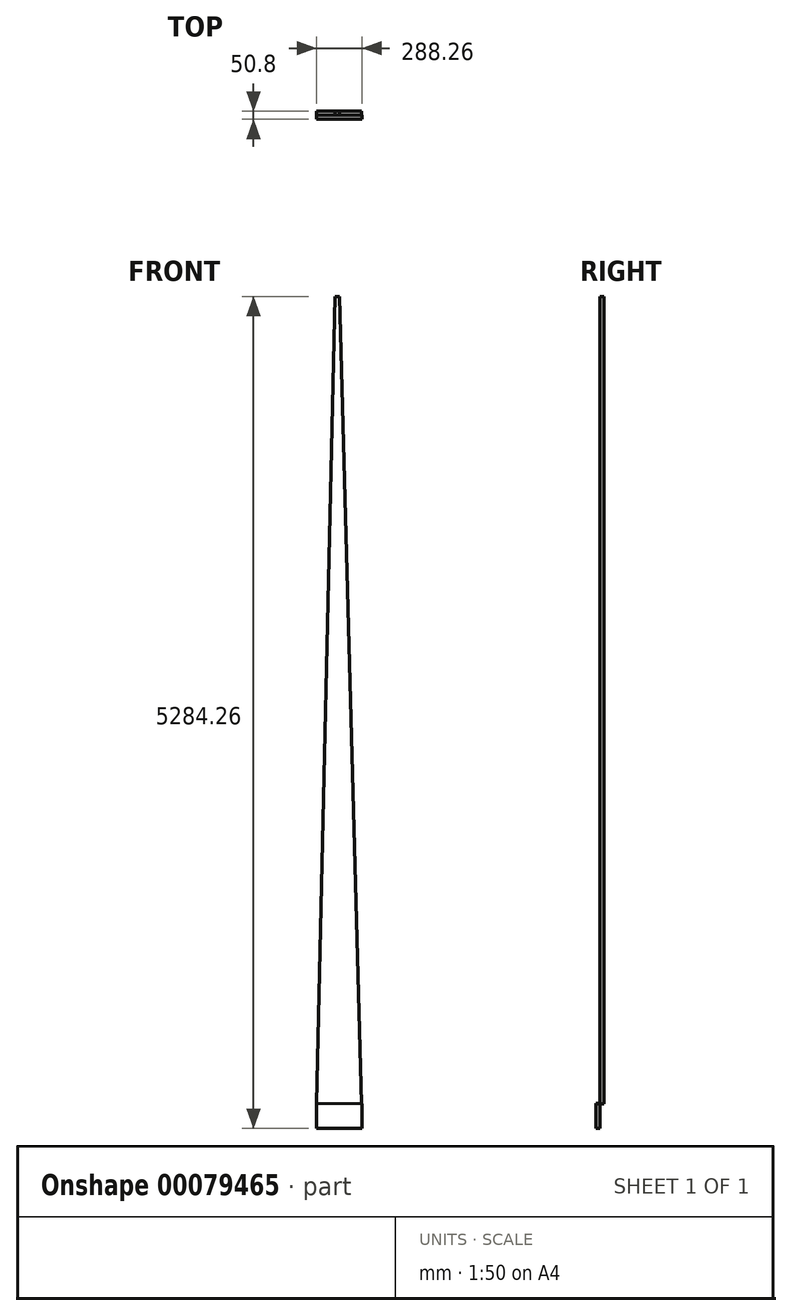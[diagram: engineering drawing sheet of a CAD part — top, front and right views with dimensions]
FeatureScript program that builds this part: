
annotation { "Feature Type Name" : "Feature", "Feature Type Description" : "" }
export const myFeature = defineFeature(function(context is Context, id is Id, definition is map)
    precondition{}
    {
        {
            var Q0;
            Q0=qCreatedBy(makeId("Front.planeOp"),FACE);
            var sketch = newSketch(context, id + "F0", { "sketchPlane" : qUnion([Q0])});
            skLineSegment(sketch, "E0", {"start": v(-145.66, 80.98) * mm, "end": v(-145.66, -77.37) * mm});
            skLineSegment(sketch, "E1", {"start": v(-145.66, -77.37) * mm, "end": v(142.6, -77.37) * mm});
            skLineSegment(sketch, "E2", {"start": v(142.6, -77.37) * mm, "end": v(142.6, 77.56) * mm});
            skLineSegment(sketch, "E3", {"start": v(142.6, 77.56) * mm, "end": v(-145.66, 80.98) * mm});
            skSolve(sketch);
        }
        {
            var Q0;
            Q0=makeQuery(id+"F0.imprint","IMPRINT",FACE,{"disambiguationData":[TD([[makeQuery(id+"F0.imprint","IMPRINT",EDGE,{"derivedFrom":sQuery(id+"F0.wireOp",EDGE,"E0")}),1.0]])]});
            extrude(context, id + "F1", {"entities" : qUnion([Q0]), "depth" : 25.4 * mm});
        }
        {
            var Q0;
            Q0=makeQuery(id+"F1.opExtrude","CAP_FACE",FACE,{"disambiguationData":[OSD([sQuery(id+"F0.wireOp",EDGE,"E0"),sQuery(id+"F0.wireOp",EDGE,"E1"),sQuery(id+"F0.wireOp",EDGE,"E2"),sQuery(id+"F0.wireOp",EDGE,"E3")])],"isStart":true});
            var sketch = newSketch(context, id + "F2", { "sketchPlane" : qUnion([Q0])});
            skLineSegment(sketch, "E4", {"start": v(145.66, 80.98) * mm, "end": v(27.63, 5237.06) * mm});
            skLineSegment(sketch, "E5", {"start": v(1.2, 5206.9) * mm, "end": v(-142.6, -77.37) * mm});
            skLineSegment(sketch, "E6", {"start": v(-142.6, -77.37) * mm, "end": v(28.32, 5206.9) * mm});
            skLineSegment(sketch, "E7", {"start": v(28.32, 5206.9) * mm, "end": v(1.2, 5206.9) * mm});
            skLineSegment(sketch, "E8", {"start": v(145.66, -77.37) * mm, "end": v(1.2, 5206.9) * mm});
            skSolve(sketch);
        }
        {
            var Q0;
            {var subQ0=sQuery(id+"F2.wireOp",EDGE,"E8");var subQ1=sQuery(id+"F2.wireOp",EDGE,"E6");var subQ2=makeQuery(id+"F2.imprint","INTERSECT",VERTEX,{"derivedFrom":[subQ1,subQ0]});Q0=makeQuery(id+"F2.imprint","IMPRINT",FACE,{"disambiguationData":[TD([[makeQuery(id+"F2.imprint","IMPRINT",EDGE,{"disambiguationData":[TD([[subQ2,1.0]])],"derivedFrom":subQ1}),-1.0]])]});}
            var Q1;
            {var subQ0=sQuery(id+"F2.wireOp",EDGE,"E8");var subQ5=sQuery(id+"F2.wireOp",EDGE,"E6");var subQ6=makeQuery(id+"F2.imprint","INTERSECT",VERTEX,{"derivedFrom":[subQ5,subQ0]});Q1=makeQuery(id+"F2.imprint","IMPRINT",FACE,{"disambiguationData":[TD([[makeQuery(id+"F2.imprint","IMPRINT",EDGE,{"disambiguationData":[TD([[subQ6,1.0]])],"derivedFrom":subQ5}),1.0]])]});}
            var Q2;
            {var subQ0=sQuery(id+"F2.wireOp",EDGE,"E7");Q2=makeQuery(id+"F2.imprint","IMPRINT",FACE,{"disambiguationData":[TD([[makeQuery(id+"F2.imprint","IMPRINT",EDGE,{"derivedFrom":subQ0}),1.0]])]});}
            var Q3;
            {var subQ3=sQuery(id+"F2.wireOp",EDGE,"E6");var subQ5=sQuery(id+"F2.wireOp",EDGE,"E8");var subQ6=makeQuery(id+"F2.imprint","INTERSECT",VERTEX,{"derivedFrom":[subQ3,subQ5]});Q3=makeQuery(id+"F2.imprint","IMPRINT",FACE,{"disambiguationData":[TD([[makeQuery(id+"F2.imprint","IMPRINT",EDGE,{"disambiguationData":[TD([[subQ6,1.0]])],"derivedFrom":subQ5}),-1.0]])]});}
            extrude(context, id + "F3", {"entities" : qUnion([Q0, Q1, Q2, Q3]), "depth" : 25.4 * mm});
        }
    });
